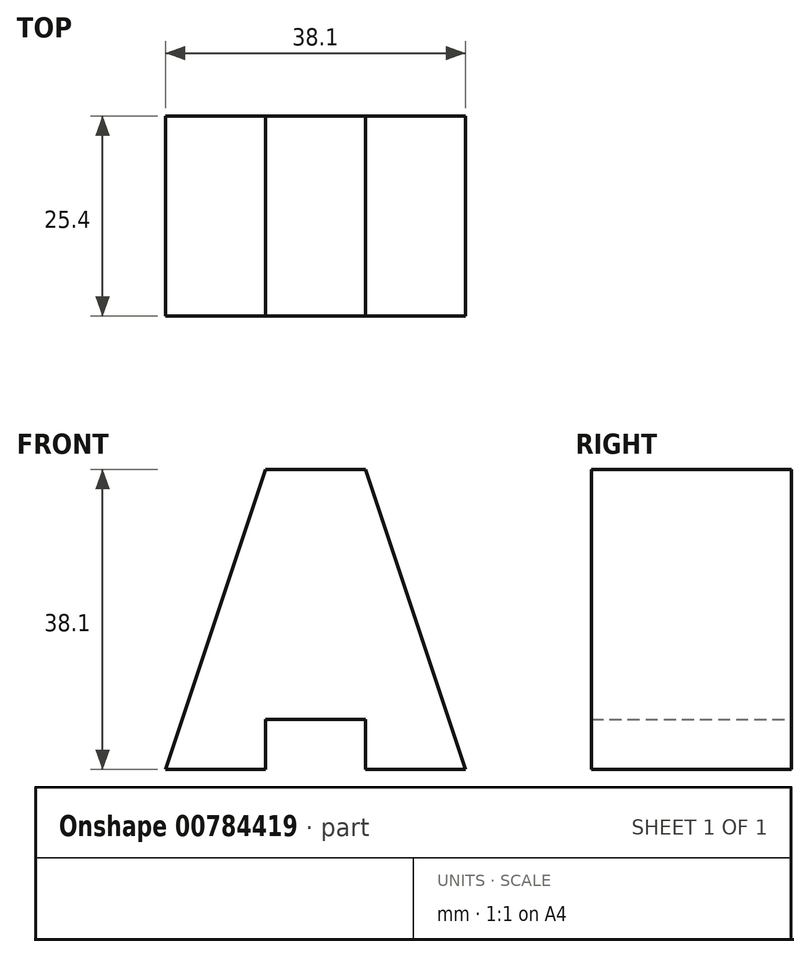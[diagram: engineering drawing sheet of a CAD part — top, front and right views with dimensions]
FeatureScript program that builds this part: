
annotation { "Feature Type Name" : "Feature", "Feature Type Description" : "" }
export const myFeature = defineFeature(function(context is Context, id is Id, definition is map)
    precondition{}
    {
        {
            var Q0;
            Q0=qCreatedBy(makeId("Front.planeOp"),FACE);
            var sketch = newSketch(context, id + "F0", { "sketchPlane" : qUnion([Q0])});
            skLineSegment(sketch, "E0", {"start": v(0, 0) * mm, "end": v(12.7, 0) * mm});
            skLineSegment(sketch, "E1", {"start": v(12.7, 0) * mm, "end": v(12.7, 6.35) * mm});
            skLineSegment(sketch, "E2", {"start": v(12.7, 6.35) * mm, "end": v(25.4, 6.35) * mm});
            skLineSegment(sketch, "E3", {"start": v(25.4, 6.35) * mm, "end": v(25.4, 0) * mm});
            skLineSegment(sketch, "E4", {"start": v(25.4, 0) * mm, "end": v(38.1, 0) * mm});
            skLineSegment(sketch, "E5", {"start": v(38.1, 0) * mm, "end": v(38.1, 38.1) * mm});
            skLineSegment(sketch, "E6", {"start": v(38.1, 38.1) * mm, "end": v(0, 38.1) * mm});
            skLineSegment(sketch, "E7", {"start": v(0, 38.1) * mm, "end": v(0, 0) * mm});
            skSolve(sketch);
        }
        {
            var Q0;
            Q0=makeQuery(id+"F0.imprint","IMPRINT",FACE,{"disambiguationData":[TD([[makeQuery(id+"F0.imprint","IMPRINT",EDGE,{"derivedFrom":sQuery(id+"F0.wireOp",EDGE,"E0")}),1.0]])]});
            extrude(context, id + "F1", {"entities" : qUnion([Q0]), "depth" : 25.4 * mm, "offsetDistance" : 25.4 * mm});
        }
        {
            var Q0;
            Q0=makeQuery(id+"F1.opExtrude","CAP_FACE",FACE,{"disambiguationData":[OSD([sQuery(id+"F0.wireOp",EDGE,"E0"),sQuery(id+"F0.wireOp",EDGE,"E1"),sQuery(id+"F0.wireOp",EDGE,"E2"),sQuery(id+"F0.wireOp",EDGE,"E3"),sQuery(id+"F0.wireOp",EDGE,"E4"),sQuery(id+"F0.wireOp",EDGE,"E5"),sQuery(id+"F0.wireOp",EDGE,"E6"),sQuery(id+"F0.wireOp",EDGE,"E7")])],"isStart":false});
            var sketch = newSketch(context, id + "F2", { "sketchPlane" : qUnion([Q0])});
            skLineSegment(sketch, "E8", {"start": v(0, 38.1) * mm, "end": v(12.7, 38.1) * mm});
            skLineSegment(sketch, "E9", {"start": v(12.7, 38.1) * mm, "end": v(0, 0) * mm});
            skLineSegment(sketch, "E10", {"start": v(38.1, 38.1) * mm, "end": v(25.4, 38.1) * mm});
            skLineSegment(sketch, "E11", {"start": v(25.4, 38.1) * mm, "end": v(38.1, 0) * mm});
            skSolve(sketch);
        }
        {
            var Q0;
            Q0=makeQuery(id+"F2.imprint","IMPRINT",FACE,{"disambiguationData":[TD([[makeQuery(id+"F2.imprint","IMPRINT",EDGE,{"derivedFrom":sQuery(id+"F2.wireOp",EDGE,"E10")}),1.0]])]});
            extrude(context, id + "F3", {"entities" : qUnion([Q0]), "operationType" : NewBodyOperationType.REMOVE, "oppositeDirection" : true, "depth" : 25.4 * mm, "offsetDistance" : 25.4 * mm});
        }
        {
            var Q0;
            Q0=makeQuery(id+"F1.opExtrude","CAP_FACE",FACE,{"disambiguationData":[OSD([sQuery(id+"F0.wireOp",EDGE,"E0"),sQuery(id+"F0.wireOp",EDGE,"E1"),sQuery(id+"F0.wireOp",EDGE,"E2"),sQuery(id+"F0.wireOp",EDGE,"E3"),sQuery(id+"F0.wireOp",EDGE,"E4"),sQuery(id+"F0.wireOp",EDGE,"E5"),sQuery(id+"F0.wireOp",EDGE,"E6"),sQuery(id+"F0.wireOp",EDGE,"E7")])],"isStart":false});
            var sketch = newSketch(context, id + "F4", { "sketchPlane" : qUnion([Q0])});
            skLineSegment(sketch, "E12", {"start": v(0, 38.1) * mm, "end": v(12.7, 38.1) * mm});
            skLineSegment(sketch, "E13", {"start": v(12.7, 38.1) * mm, "end": v(0, 0) * mm});
            skSolve(sketch);
        }
        {
            var Q0;
            Q0=makeQuery(id+"F4.imprint","IMPRINT",FACE,{"disambiguationData":[TD([[makeQuery(id+"F4.imprint","IMPRINT",EDGE,{"derivedFrom":sQuery(id+"F4.wireOp",EDGE,"E12")}),1.0]])]});
            extrude(context, id + "F5", {"entities" : qUnion([Q0]), "operationType" : NewBodyOperationType.REMOVE, "oppositeDirection" : true, "depth" : 25.4 * mm, "offsetDistance" : 25.4 * mm});
        }
    });
